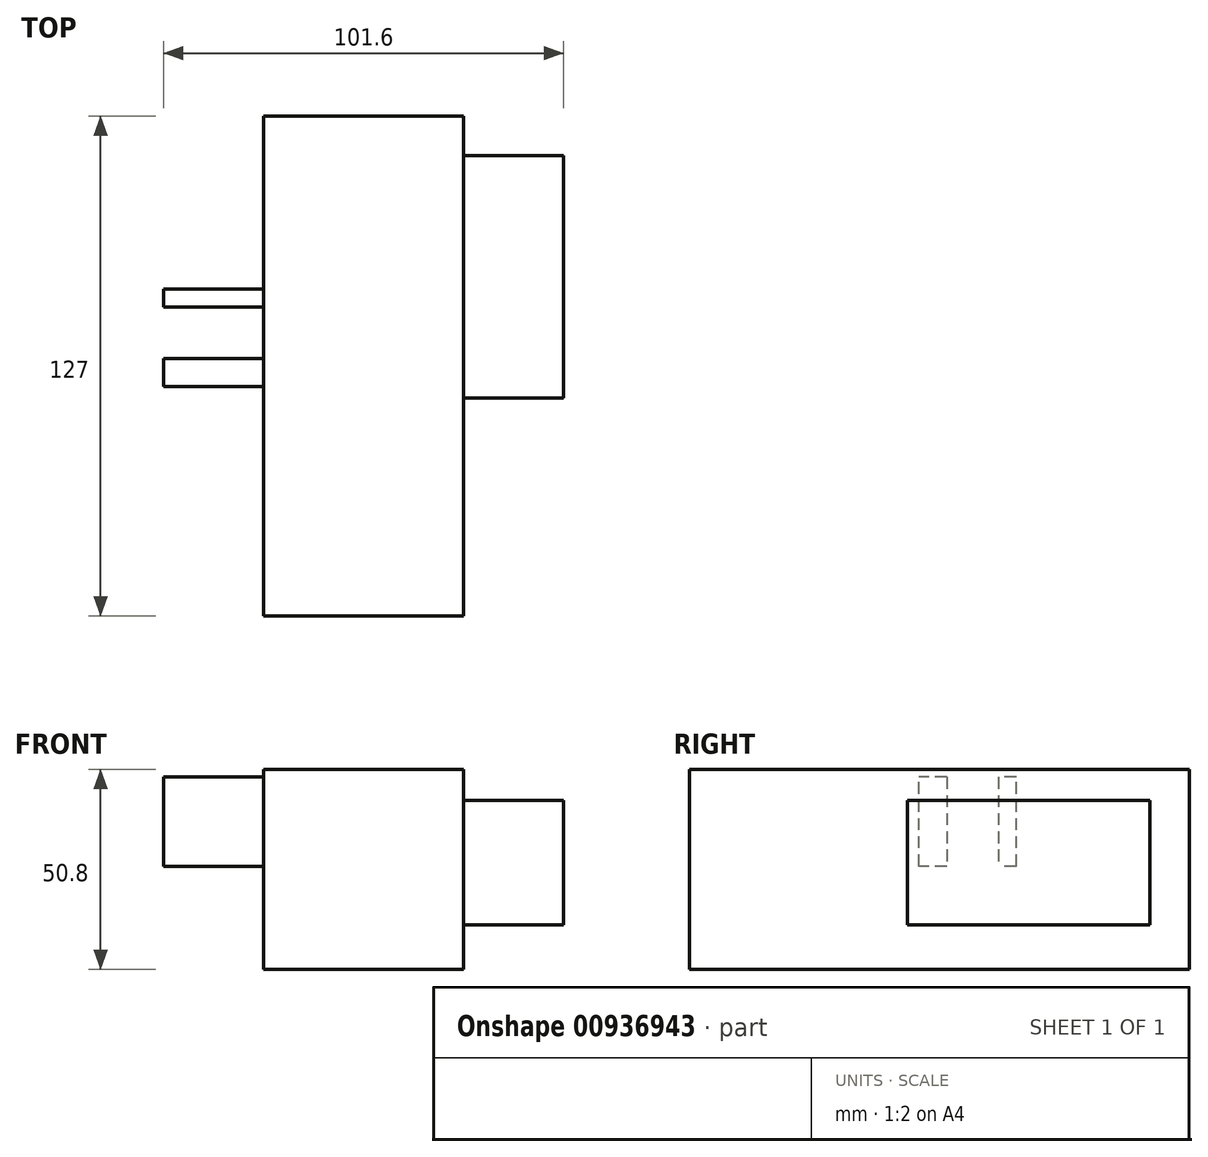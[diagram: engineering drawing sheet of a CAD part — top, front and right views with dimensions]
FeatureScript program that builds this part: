
annotation { "Feature Type Name" : "Feature", "Feature Type Description" : "" }
export const myFeature = defineFeature(function(context is Context, id is Id, definition is map)
    precondition{}
    {
        {
            var Q0;
            Q0=qCreatedBy(makeId("Front.planeOp"),FACE);
            var sketch = newSketch(context, id + "F0", { "sketchPlane" : qUnion([Q0])});
            skLineSegment(sketch, "E0.bottom", {"start": v(14.78, 24.58) * mm, "end": v(-36.02, 24.58) * mm});
            skLineSegment(sketch, "E0.top", {"start": v(14.78, -26.22) * mm, "end": v(-36.02, -26.22) * mm});
            skLineSegment(sketch, "E0.left", {"start": v(14.78, 24.58) * mm, "end": v(14.78, -26.22) * mm});
            skLineSegment(sketch, "E0.right", {"start": v(-36.02, 24.58) * mm, "end": v(-36.02, -26.22) * mm});
            skSolve(sketch);
        }
        {
            var Q0;
            Q0=makeQuery(id+"F0.imprint","IMPRINT",FACE,{"disambiguationData":[TD([[makeQuery(id+"F0.imprint","IMPRINT",EDGE,{"derivedFrom":sQuery(id+"F0.wireOp",EDGE,"E0.bottom")}),1.0]])]});
            extrude(context, id + "F1", {"entities" : qUnion([Q0]), "depth" : 127 * mm, "offsetDistance" : 25.4 * mm});
        }
        {
            var Q0;
            Q0=makeQuery(id+"F1.opExtrude","SWEPT_FACE",FACE,{"disambiguationData":[OSD([sQuery(id+"F0.wireOp",EDGE,"E0.left")])]});
            var sketch = newSketch(context, id + "F2", { "sketchPlane" : qUnion([Q0])});
            skLineSegment(sketch, "E1.bottom", {"start": v(-71.6, -14.93) * mm, "end": v(-10.05, -14.93) * mm});
            skLineSegment(sketch, "E1.top", {"start": v(-71.6, 16.76) * mm, "end": v(-10.05, 16.76) * mm});
            skLineSegment(sketch, "E1.left", {"start": v(-71.6, -14.93) * mm, "end": v(-71.6, 16.76) * mm});
            skLineSegment(sketch, "E1.right", {"start": v(-10.05, -14.93) * mm, "end": v(-10.05, 16.76) * mm});
            skSolve(sketch);
        }
        {
            var Q0;
            Q0=makeQuery(id+"F2.imprint","IMPRINT",FACE,{"disambiguationData":[TD([[makeQuery(id+"F2.imprint","IMPRINT",EDGE,{"derivedFrom":sQuery(id+"F2.wireOp",EDGE,"E1.bottom")}),1.0]])]});
            extrude(context, id + "F3", {"entities" : qUnion([Q0]), "operationType" : NewBodyOperationType.ADD, "endBound" : BoundingType.SYMMETRIC, "oppositeDirection" : true, "depth" : 50.8 * mm, "offsetDistance" : 25.4 * mm});
        }
        {
            var Q0;
            Q0=makeQuery(id+"F1.opExtrude","SWEPT_FACE",FACE,{"disambiguationData":[OSD([sQuery(id+"F0.wireOp",EDGE,"E0.right")])]});
            var sketch = newSketch(context, id + "F4", { "sketchPlane" : qUnion([Q0])});
            skLineSegment(sketch, "E2.bottom", {"start": v(43.99, 0) * mm, "end": v(68.67, 0) * mm});
            skLineSegment(sketch, "E2.top", {"start": v(43.99, 22.65) * mm, "end": v(68.67, 22.65) * mm});
            skLineSegment(sketch, "E2.left", {"start": v(43.99, 0) * mm, "end": v(43.99, 22.65) * mm});
            skLineSegment(sketch, "E2.right", {"start": v(68.67, 0) * mm, "end": v(68.67, 22.65) * mm});
            skPoint(sketch, "E2.middle", {"position": v(56.33, 11.32) * mm});
            skLineSegment(sketch, "E3", {"start": v(61.6, 22.65) * mm, "end": v(61.6, 0) * mm});
            skLineSegment(sketch, "E4", {"start": v(61.6, 0) * mm, "end": v(56.33, 22.65) * mm});
            skLineSegment(sketch, "E5", {"start": v(56.33, 22.65) * mm, "end": v(56.71, -0.24) * mm});
            skLineSegment(sketch, "E6", {"start": v(56.71, -0.24) * mm, "end": v(48.55, 22.65) * mm});
            skLineSegment(sketch, "E7", {"start": v(48.55, 22.65) * mm, "end": v(48.55, 0) * mm});
            skSolve(sketch);
        }
        {
            var Q0;
            {var subQ0=sQuery(id+"F4.wireOp",EDGE,"E2.left");Q0=makeQuery(id+"F4.imprint","IMPRINT",FACE,{"disambiguationData":[TD([[makeQuery(id+"F4.imprint","IMPRINT",EDGE,{"derivedFrom":subQ0}),-1.0]])]});}
            extrude(context, id + "F5", {"entities" : qUnion([Q0]), "operationType" : NewBodyOperationType.ADD, "depth" : 25.4 * mm, "offsetDistance" : 25.4 * mm});
        }
        {
            var Q0;
            {var subQ0=sQuery(id+"F4.wireOp",EDGE,"E2.right");Q0=makeQuery(id+"F4.imprint","IMPRINT",FACE,{"disambiguationData":[TD([[makeQuery(id+"F4.imprint","IMPRINT",EDGE,{"derivedFrom":subQ0}),1.0]])]});}
            extrude(context, id + "F6", {"entities" : qUnion([Q0]), "operationType" : NewBodyOperationType.ADD, "depth" : 25.4 * mm, "offsetDistance" : 25.4 * mm});
        }
    });
